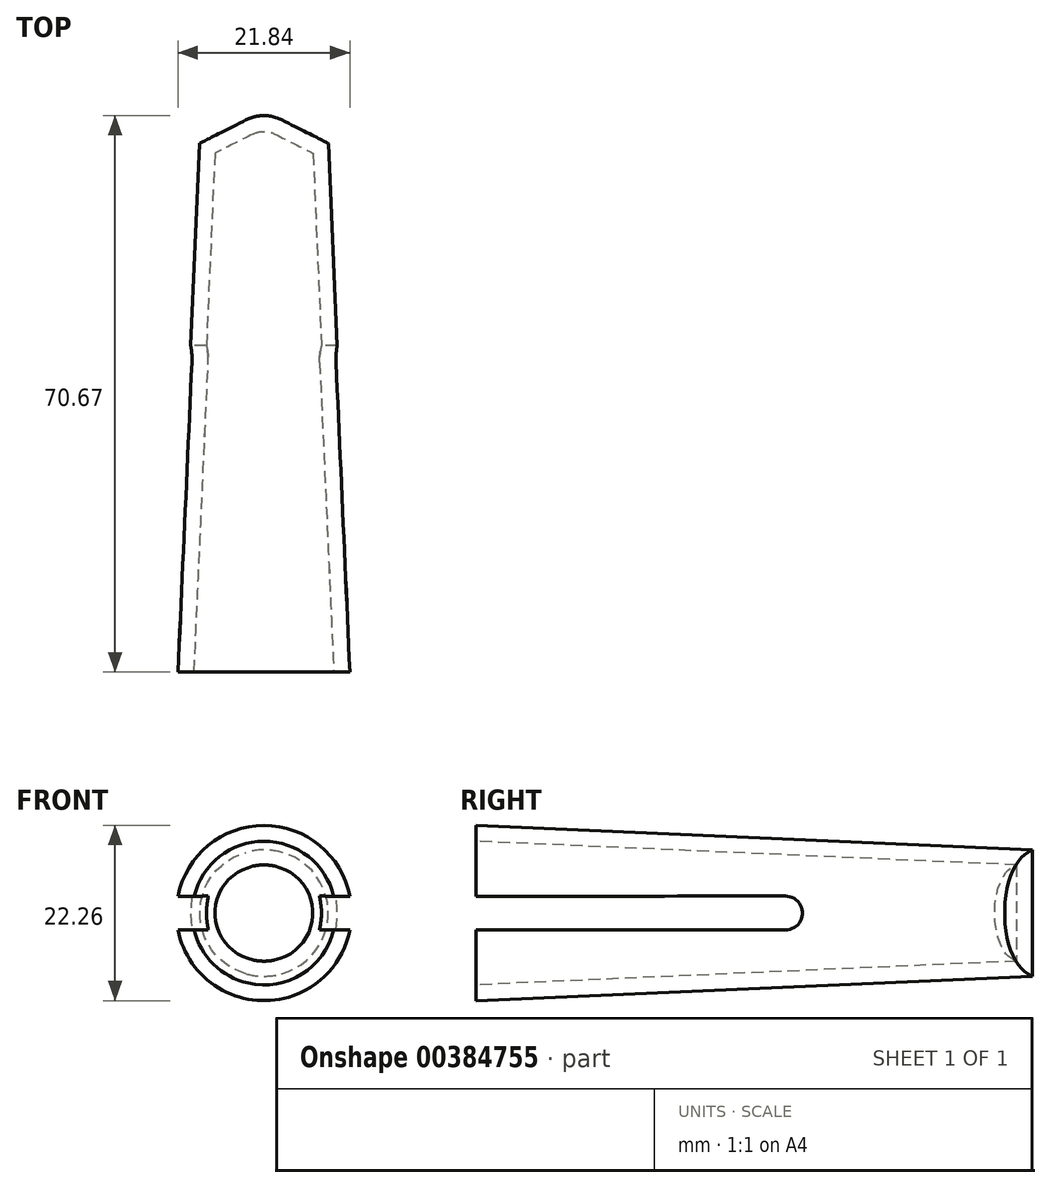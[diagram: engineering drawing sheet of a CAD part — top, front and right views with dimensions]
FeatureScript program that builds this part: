
annotation { "Feature Type Name" : "Feature", "Feature Type Description" : "" }
export const myFeature = defineFeature(function(context is Context, id is Id, definition is map)
    precondition{}
    {
        {
            var Q0;
            Q0=qCreatedBy(makeId("Top.planeOp"),FACE);
            var sketch = newSketch(context, id + "F0", { "sketchPlane" : qUnion([Q0])});
            skLineSegment(sketch, "E0", {"start": v(-8, 0) * mm, "end": v(0, 0) * mm});
            skLineSegment(sketch, "E1", {"start": v(-8, 0) * mm, "end": v(-11.13, -71.27) * mm});
            skLineSegment(sketch, "E2", {"start": v(-11.13, -71.27) * mm, "end": v(0, -71.27) * mm});
            skLineSegment(sketch, "E3", {"start": v(0, -71.27) * mm, "end": v(0, 0) * mm});
            skSolve(sketch);
        }
        {
            var Q0;
            Q0=qCreatedBy(makeId("Top.planeOp"),FACE);
            var sketch = newSketch(context, id + "F1", { "sketchPlane" : qUnion([Q0])});
            skLineSegment(sketch, "E4", {"start": v(0, -70.6) * mm, "end": v(0, 43.47) * mm, "construction": true});
            skSolve(sketch);
        }
        {
            var Q0;
            Q0=makeQuery(id+"F0.imprint","IMPRINT",FACE,{"disambiguationData":[TD([[makeQuery(id+"F0.imprint","IMPRINT",EDGE,{"derivedFrom":sQuery(id+"F0.wireOp",EDGE,"E0")}),-1.0]])]});
            var Q1;
            Q1=sQuery(id+"F1.wireOp",EDGE,"E4");
            revolve(context, id + "F2", {"entities" : qUnion([Q0]), "axis" : qUnion([Q1]), "revolveType" : RevolveType.FULL});
        }
        {
            var Q0;
            Q0=qCreatedBy(makeId("Top.planeOp"),FACE);
            var sketch = newSketch(context, id + "F3", { "sketchPlane" : qUnion([Q0])});
            skLineSegment(sketch, "E5", {"start": v(0, 0) * mm, "end": v(-12.45, -6.27) * mm});
            skLineSegment(sketch, "E6.MirrorCS", {"start": v(0, 0) * mm, "end": v(12.45, -6.27) * mm});
            skPoint(sketch, "E7.end.orphan", {"position": v(0, 6.47) * mm});
            skLineSegment(sketch, "E8", {"start": v(-12.45, -6.27) * mm, "end": v(-16.84, 5.98) * mm});
            skLineSegment(sketch, "E9", {"start": v(-16.84, 5.98) * mm, "end": v(0, 11.9) * mm});
            skLineSegment(sketch, "E10", {"start": v(0, 11.9) * mm, "end": v(16.58, 8.64) * mm});
            skLineSegment(sketch, "E11", {"start": v(16.58, 8.64) * mm, "end": v(12.45, -6.27) * mm});
            skSolve(sketch);
        }
        {
            var Q0;
            Q0=makeQuery(id+"F3.imprint","IMPRINT",FACE,{"disambiguationData":[TD([[makeQuery(id+"F3.imprint","IMPRINT",EDGE,{"derivedFrom":sQuery(id+"F3.wireOp",EDGE,"E5")}),-1.0]])]});
            extrude(context, id + "F4", {"entities" : qUnion([Q0]), "operationType" : NewBodyOperationType.REMOVE, "oppositeDirection" : true, "depth" : 25 * mm, "hasSecondDirection" : true, "secondDirectionBound" : SecondDirectionBoundingType.THROUGH_ALL, "secondDirectionOppositeDirection" : false, "secondDirectionDepth" : 25 * mm});
        }
        {
            var Q0;
            Q0=makeQuery(id+"F4.boolean.opBoolean","COPY",EDGE,{"derivedFrom":makeQuery(id+"F4.opExtrude","SWEPT_EDGE",EDGE,{"disambiguationData":[OSD([sQuery(id+"F3.wireOp",EDGE,"E5"),sQuery(id+"F3.wireOp",EDGE,"E6.MirrorCS")])]})});
            fillet(context, id + "F5", {"entities" : qUnion([Q0]), "radius" : 5 * mm, "tangentPropagation" : true, "allowEdgeOverflow" : false});
        }
        {
            var Q0;
            Q0=makeQuery(id+"F2.opRevolve","SWEPT_FACE",FACE,{"disambiguationData":[OSD([sQuery(id+"F0.wireOp",EDGE,"E2")])]});
            shell(context, id + "F6", {"entities" : qUnion([Q0]), "thickness" : 2 * mm});
        }
        {
            var Q0;
            Q0=qCreatedBy(makeId("Right.planeOp"),FACE);
            var sketch = newSketch(context, id + "F7", { "sketchPlane" : qUnion([Q0])});
            skArc(sketch, "E12", {"start": v(-31.96, -2.16) * mm, "mid": v(-29.8, 0) * mm, "end": v(-31.96, 2.16) * mm});
            skLineSegment(sketch, "E13", {"start": v(-31.96, -2.16) * mm, "end": v(-72.45, -2.15) * mm});
            skLineSegment(sketch, "E14.MirrorCS", {"start": v(-31.96, 2.16) * mm, "end": v(-72.45, 2.13) * mm});
            skPoint(sketch, "E15.start.orphan", {"position": v(-73.6, -2.15) * mm});
            skLineSegment(sketch, "E16", {"start": v(-72.45, -2.15) * mm, "end": v(-72.45, 2.13) * mm});
            skSolve(sketch);
        }
        {
            var Q0;
            Q0 = qSketchRegion(id + "F7", true);
            extrude(context, id + "F8", {"entities" : qUnion([Q0]), "operationType" : NewBodyOperationType.REMOVE, "depth" : 25 * mm, "hasSecondDirection" : true, "secondDirectionOppositeDirection" : true, "secondDirectionDepth" : 25 * mm});
        }
    });
